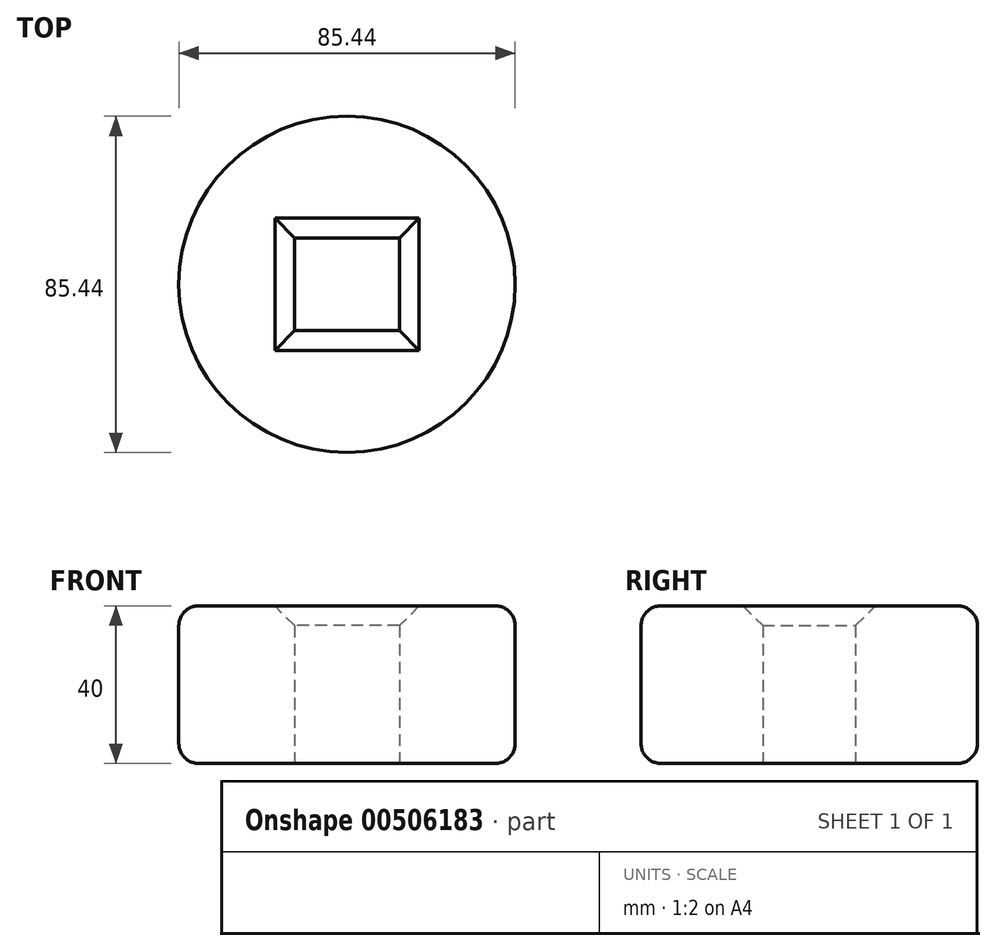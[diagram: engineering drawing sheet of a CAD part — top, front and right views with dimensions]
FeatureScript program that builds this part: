
annotation { "Feature Type Name" : "Feature", "Feature Type Description" : "" }
export const myFeature = defineFeature(function(context is Context, id is Id, definition is map)
    precondition{}
    {
        {
            var Q0;
            Q0=qCreatedBy(makeId("Top.planeOp"),FACE);
            var sketch = newSketch(context, id + "F0", { "sketchPlane" : qUnion([Q0])});
            skCircle(sketch, "E0", {"center": v(0, 0) * mm, "radius": 42.72 * mm});
            skSolve(sketch);
        }
        {
            var Q0;
            Q0 = qSketchRegion(id + "F0", true);
            extrude(context, id + "F1", {"entities" : qUnion([Q0]), "depth" : 40 * mm});
        }
        {
            var Q0;
            Q0=qCreatedBy(makeId("Top.planeOp"),FACE);
            var sketch = newSketch(context, id + "F2", { "sketchPlane" : qUnion([Q0])});
            skLineSegment(sketch, "E1.bottom", {"start": v(13.33, 11.78) * mm, "end": v(-13.33, 11.78) * mm});
            skLineSegment(sketch, "E1.top", {"start": v(13.33, -11.78) * mm, "end": v(-13.33, -11.78) * mm});
            skLineSegment(sketch, "E1.left", {"start": v(13.33, 11.78) * mm, "end": v(13.33, -11.78) * mm});
            skLineSegment(sketch, "E1.right", {"start": v(-13.33, 11.78) * mm, "end": v(-13.33, -11.78) * mm});
            skPoint(sketch, "E1.middle", {"position": v(0, 0) * mm});
            skSolve(sketch);
        }
        {
            var Q0;
            Q0 = qSketchRegion(id + "F2", true);
            extrude(context, id + "F3", {"entities" : qUnion([Q0]), "operationType" : NewBodyOperationType.REMOVE, "endBound" : BoundingType.THROUGH_ALL, "depth" : 25 * mm});
        }
        {
            var Q0;
            Q0=makeQuery(id+"F3.boolean.opBoolean","INTERSECT",EDGE,{"derivedFrom":[makeQuery(id+"F1.opExtrude","CAP_FACE",FACE,{"disambiguationData":[OSD([sQuery(id+"F0.wireOp",EDGE,"E0")])],"isStart":false}),makeQuery(id+"F3.opExtrude","SWEPT_FACE",FACE,{"disambiguationData":[OSD([sQuery(id+"F2.wireOp",EDGE,"E1.bottom")])]})]});
            var Q1;
            Q1=makeQuery(id+"F3.boolean.opBoolean","INTERSECT",EDGE,{"derivedFrom":[makeQuery(id+"F1.opExtrude","CAP_FACE",FACE,{"disambiguationData":[OSD([sQuery(id+"F0.wireOp",EDGE,"E0")])],"isStart":false}),makeQuery(id+"F3.opExtrude","SWEPT_FACE",FACE,{"disambiguationData":[OSD([sQuery(id+"F2.wireOp",EDGE,"E1.left")])]})]});
            var Q2;
            Q2=makeQuery(id+"F3.boolean.opBoolean","INTERSECT",EDGE,{"derivedFrom":[makeQuery(id+"F1.opExtrude","CAP_FACE",FACE,{"disambiguationData":[OSD([sQuery(id+"F0.wireOp",EDGE,"E0")])],"isStart":false}),makeQuery(id+"F3.opExtrude","SWEPT_FACE",FACE,{"disambiguationData":[OSD([sQuery(id+"F2.wireOp",EDGE,"E1.right")])]})]});
            var Q3;
            Q3=makeQuery(id+"F3.boolean.opBoolean","INTERSECT",EDGE,{"derivedFrom":[makeQuery(id+"F1.opExtrude","CAP_FACE",FACE,{"disambiguationData":[OSD([sQuery(id+"F0.wireOp",EDGE,"E0")])],"isStart":false}),makeQuery(id+"F3.opExtrude","SWEPT_FACE",FACE,{"disambiguationData":[OSD([sQuery(id+"F2.wireOp",EDGE,"E1.top")])]})]});
            chamfer(context, id + "F4", {"entities" : qUnion([Q0, Q1, Q2, Q3]), "width" : 5 * mm, "tangentPropagation" : true});
        }
        {
            var Q0;
            Q0=makeQuery(id+"F1.opExtrude","CAP_EDGE",EDGE,{"disambiguationData":[OSD([sQuery(id+"F0.wireOp",EDGE,"E0")])],"isStart":false});
            fillet(context, id + "F5", {"entities" : qUnion([Q0]), "radius" : 5 * mm, "tangentPropagation" : true, "allowEdgeOverflow" : false});
        }
        {
            var Q0;
            Q0=makeQuery(id+"F1.opExtrude","CAP_EDGE",EDGE,{"disambiguationData":[OSD([sQuery(id+"F0.wireOp",EDGE,"E0")])],"isStart":true});
            fillet(context, id + "F6", {"entities" : qUnion([Q0]), "radius" : 5 * mm, "tangentPropagation" : true, "allowEdgeOverflow" : false});
        }
    });
